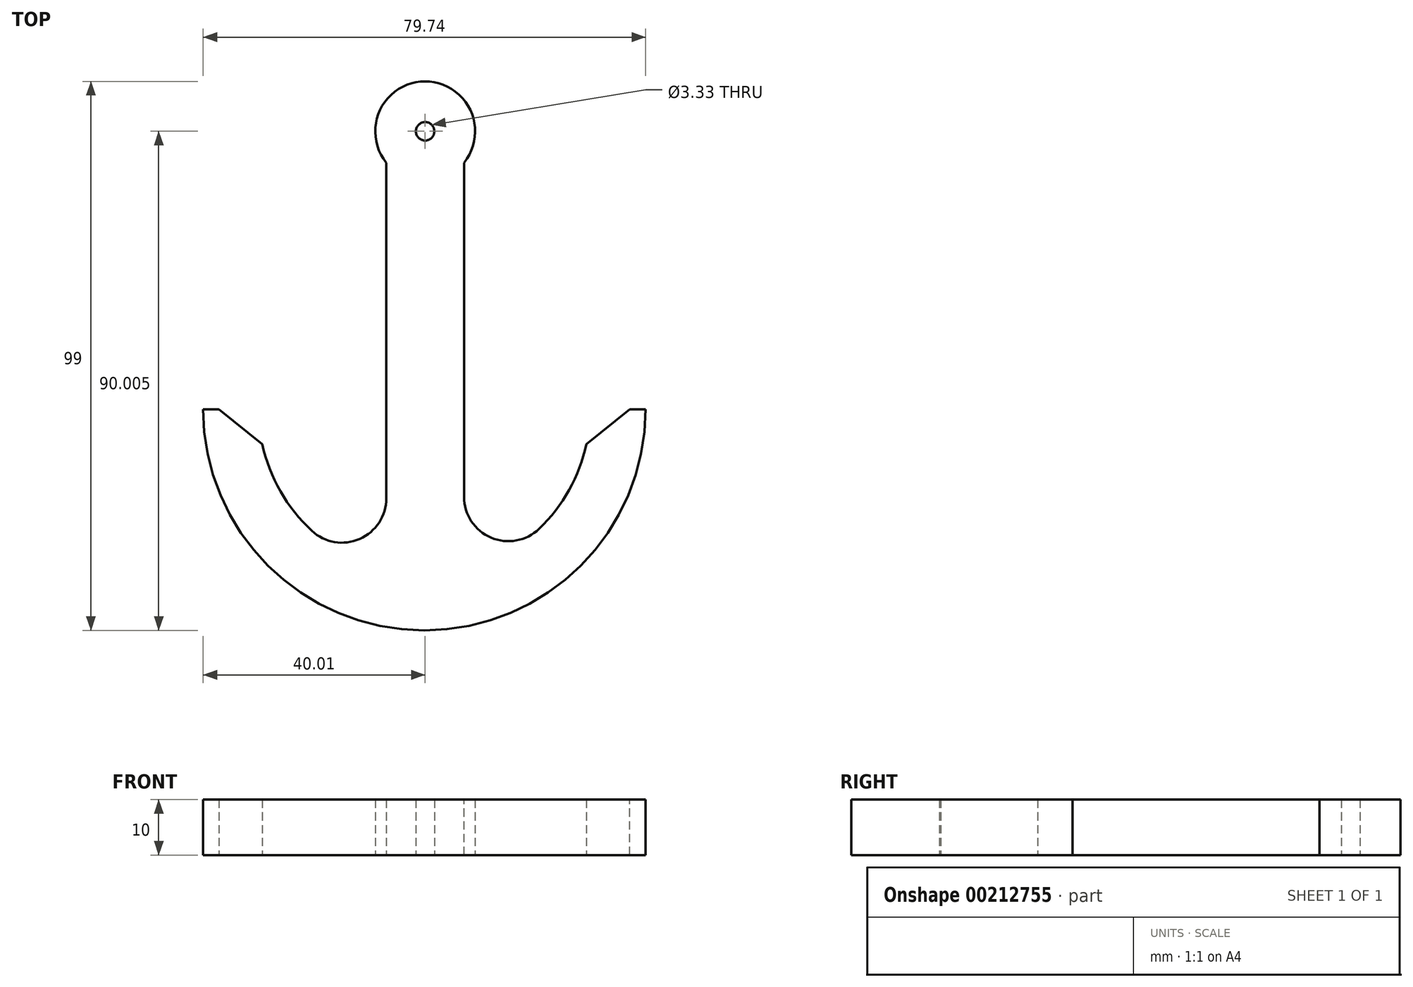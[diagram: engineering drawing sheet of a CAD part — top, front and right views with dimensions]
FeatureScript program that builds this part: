
annotation { "Feature Type Name" : "Feature", "Feature Type Description" : "" }
export const myFeature = defineFeature(function(context is Context, id is Id, definition is map)
    precondition{}
    {
        {
            assignVariable(context, id + "F0", {"name" : "w", "anyValue" : 10});
        }
        {
            var Q0;
            Q0=qCreatedBy(makeId("Top.planeOp"),FACE);
            var sketch = newSketch(context, id + "F1", { "sketchPlane" : qUnion([Q0])});
            skLineSegment(sketch, "E0.bottom", {"start": v(-7, 48.96) * mm, "end": v(7, 48.96) * mm});
            skLineSegment(sketch, "E0.left", {"start": v(-7, 48.96) * mm, "end": v(-7, -35.9) * mm});
            skLineSegment(sketch, "E0.right", {"start": v(7, 48.96) * mm, "end": v(7, -35.83) * mm});
            skCircle(sketch, "E1", {"center": v(0, 43.3) * mm, "radius": 9 * mm});
            skPoint(sketch, "E1.centerSnap0", {"position": v(0, 48.96) * mm});
            skCircle(sketch, "E2", {"center": v(0, 43.3) * mm, "radius": 1.67 * mm});
            skLineSegment(sketch, "E3", {"start": v(39.73, -6.82) * mm, "end": v(39.73, -6.82) * mm});
            skPoint(sketch, "E4", {"position": v(0, -46.7) * mm});
            skPoint(sketch, "E5", {"position": v(-40.01, -6.82) * mm});
            skLineSegment(sketch, "E6", {"start": v(-39.64, -6.82) * mm, "end": v(-40.01, -6.82) * mm});
            skArc(sketch, "E7", {"start": v(-40.01, -6.82) * mm, "mid": v(-0.14, -46.7) * mm, "end": v(39.73, -6.82) * mm});
            skLineSegment(sketch, "E8", {"start": v(-30.01, -6.82) * mm, "end": v(-39.64, -6.82) * mm});
            skArc(sketch, "E9", {"start": v(-30.01, -6.82) * mm, "mid": v(-0.14, -36.7) * mm, "end": v(29.73, -6.82) * mm});
            skLineSegment(sketch, "E10", {"start": v(29.73, -6.82) * mm, "end": v(39.73, -6.82) * mm});
            skPoint(sketch, "E11", {"position": v(-0.14, -36.7) * mm});
            skSolve(sketch);
        }
        {
            var Q0;
            {var subQ5=sQuery(id+"F1.wireOp",EDGE,"E0.bottom");Q0=makeQuery(id+"F1.imprint","IMPRINT",FACE,{"disambiguationData":[TD([[makeQuery(id+"F1.imprint","IMPRINT",EDGE,{"derivedFrom":subQ5}),-1.0]])]});}
            var Q1;
            {var subQ0=sQuery(id+"F1.wireOp",EDGE,"E0.bottom");Q1=makeQuery(id+"F1.imprint","IMPRINT",FACE,{"disambiguationData":[TD([[makeQuery(id+"F1.imprint","IMPRINT",EDGE,{"derivedFrom":subQ0}),1.0]])]});}
            var Q2;
            {var subQ0=sQuery(id+"F1.wireOp",EDGE,"E1");var subQ1=sQuery(id+"F1.wireOp",EDGE,"E0.left");var subQ2=makeQuery(id+"F1.imprint","INTERSECT",VERTEX,{"derivedFrom":[subQ1,subQ0]});Q2=makeQuery(id+"F1.imprint","IMPRINT",FACE,{"disambiguationData":[TD([[makeQuery(id+"F1.imprint","IMPRINT",EDGE,{"disambiguationData":[TD([[subQ2,-1.0]])],"derivedFrom":subQ1}),1.0]])]});}
            var Q3;
            {var subQ0=sQuery(id+"F1.wireOp",EDGE,"TjiRBAFt-rIbT-Rtpd-q4Hv-UdDr9JeEh51r");var subQ1=sQuery(id+"F1.wireOp",EDGE,"E0.left");var subQ2=makeQuery(id+"F1.imprint","INTERSECT",VERTEX,{"disambiguationData":[OD(0.0)],"derivedFrom":[subQ1,subQ0]});Q3=makeQuery(id+"F1.imprint","IMPRINT",FACE,{"disambiguationData":[TD([[makeQuery(id+"F1.imprint","IMPRINT",EDGE,{"disambiguationData":[TD([[subQ2,1.0]])],"derivedFrom":subQ1}),1.0]])]});}
            var Q4;
            {var subQ0=sQuery(id+"F1.wireOp",EDGE,"TjiRBAFt-rIbT-Rtpd-q4Hv-UdDr9JeEh51r");var subQ1=sQuery(id+"F1.wireOp",EDGE,"E0.left");var subQ2=makeQuery(id+"F1.imprint","INTERSECT",VERTEX,{"disambiguationData":[OD(1.0)],"derivedFrom":[subQ1,subQ0]});Q4=makeQuery(id+"F1.imprint","IMPRINT",FACE,{"disambiguationData":[TD([[makeQuery(id+"F1.imprint","IMPRINT",EDGE,{"disambiguationData":[TD([[subQ2,-1.0]])],"derivedFrom":subQ1}),1.0]])]});}
            var Q5;
            {var subQ1=sQuery(id+"F1.wireOp",EDGE,"E0.left");var subQ5=sQuery(id+"F1.wireOp",EDGE,"KmF6qriy-v43V-YwKp-XvIB-jkBJgwhcMQSk");var subQ9=makeQuery(id+"F1.imprint","INTERSECT",VERTEX,{"derivedFrom":[subQ1,subQ5]});Q5=makeQuery(id+"F1.imprint","IMPRINT",FACE,{"disambiguationData":[TD([[makeQuery(id+"F1.imprint","IMPRINT",EDGE,{"disambiguationData":[TD([[subQ9,-1.0]])],"derivedFrom":subQ1}),1.0]])]});}
            var Q6;
            {var subQ0=sQuery(id+"F1.wireOp",EDGE,"E1");var subQ1=sQuery(id+"F1.wireOp",EDGE,"E0.right");var subQ2=makeQuery(id+"F1.imprint","INTERSECT",VERTEX,{"derivedFrom":[subQ1,subQ0]});Q6=makeQuery(id+"F1.imprint","IMPRINT",FACE,{"disambiguationData":[TD([[makeQuery(id+"F1.imprint","IMPRINT",EDGE,{"disambiguationData":[TD([[subQ2,-1.0]])],"derivedFrom":subQ1}),-1.0]])]});}
            var Q7;
            {var subQ0=sQuery(id+"F1.wireOp",EDGE,"TjiRBAFt-rIbT-Rtpd-q4Hv-UdDr9JeEh51r");var subQ1=sQuery(id+"F1.wireOp",EDGE,"E1");var subQ2=makeQuery(id+"F1.imprint","INTERSECT",VERTEX,{"disambiguationData":[OD(0.0)],"derivedFrom":[subQ1,subQ0]});Q7=makeQuery(id+"F1.imprint","IMPRINT",FACE,{"disambiguationData":[TD([[makeQuery(id+"F1.imprint","IMPRINT",EDGE,{"disambiguationData":[TD([[subQ2,-1.0]])],"derivedFrom":subQ1}),1.0]])]});}
            var Q8;
            {var subQ0=sQuery(id+"F1.wireOp",EDGE,"E3");var subQ1=sQuery(id+"F1.wireOp",EDGE,"E0.left");var subQ2=makeQuery(id+"F1.imprint","INTERSECT",VERTEX,{"derivedFrom":[subQ1,subQ0]});Q8=makeQuery(id+"F1.imprint","IMPRINT",FACE,{"disambiguationData":[TD([[makeQuery(id+"F1.imprint","IMPRINT",EDGE,{"disambiguationData":[TD([[subQ2,-1.0]])],"derivedFrom":subQ1}),1.0]])]});}
            var Q9;
            {var subQ0=sQuery(id+"F1.wireOp",EDGE,"E3");var subQ1=sQuery(id+"F1.wireOp",EDGE,"E0.right");var subQ2=makeQuery(id+"F1.imprint","INTERSECT",VERTEX,{"derivedFrom":[subQ1,subQ0]});Q9=makeQuery(id+"F1.imprint","IMPRINT",FACE,{"disambiguationData":[TD([[makeQuery(id+"F1.imprint","IMPRINT",EDGE,{"disambiguationData":[TD([[subQ2,-1.0]])],"derivedFrom":subQ1}),-1.0]])]});}
            var Q10;
            {var subQ2=sQuery(id+"F1.wireOp",EDGE,"MNqs9SMt-crvg-llG4-YDsR-waINOACBQYCp");var subQ7=sQuery(id+"F1.wireOp",EDGE,"KmF6qriy-v43V-YwKp-XvIB-jkBJgwhcMQSk");var subQ9=makeQuery(id+"F1.imprint","INTERSECT",VERTEX,{"derivedFrom":[subQ7,subQ2]});Q10=makeQuery(id+"F1.imprint","IMPRINT",FACE,{"disambiguationData":[TD([[makeQuery(id+"F1.imprint","IMPRINT",EDGE,{"disambiguationData":[TD([[subQ9,-1.0]])],"derivedFrom":subQ7}),1.0]])]});}
            var Q11;
            {var subQ2=sQuery(id+"F1.wireOp",EDGE,"E3");var subQ4=sQuery(id+"F1.wireOp",EDGE,"KmF6qriy-v43V-YwKp-XvIB-jkBJgwhcMQSk");var subQ5=makeQuery(id+"F1.imprint","INTERSECT",VERTEX,{"disambiguationData":[OD(1.0)],"derivedFrom":[subQ4,subQ2]});Q11=makeQuery(id+"F1.imprint","IMPRINT",FACE,{"disambiguationData":[TD([[makeQuery(id+"F1.imprint","IMPRINT",EDGE,{"disambiguationData":[TD([[subQ5,-1.0]])],"derivedFrom":subQ4}),1.0]])]});}
            var Q12;
            {var subQ0=sQuery(id+"F1.wireOp",EDGE,"E1");var subQ3=sQuery(id+"F1.wireOp",EDGE,"KmF6qriy-v43V-YwKp-XvIB-jkBJgwhcMQSk");var subQ5=makeQuery(id+"F1.imprint","INTERSECT",VERTEX,{"disambiguationData":[OD(1.0)],"derivedFrom":[subQ0,subQ3]});Q12=makeQuery(id+"F1.imprint","IMPRINT",FACE,{"disambiguationData":[TD([[makeQuery(id+"F1.imprint","IMPRINT",EDGE,{"disambiguationData":[TD([[subQ5,-1.0]])],"derivedFrom":subQ3}),-1.0]])]});}
            var Q13;
            {var subQ0=sQuery(id+"F1.wireOp",EDGE,"E1");var subQ3=sQuery(id+"F1.wireOp",EDGE,"KmF6qriy-v43V-YwKp-XvIB-jkBJgwhcMQSk");var subQ5=makeQuery(id+"F1.imprint","INTERSECT",VERTEX,{"disambiguationData":[OD(0.0)],"derivedFrom":[subQ0,subQ3]});Q13=makeQuery(id+"F1.imprint","IMPRINT",FACE,{"disambiguationData":[TD([[makeQuery(id+"F1.imprint","IMPRINT",EDGE,{"disambiguationData":[TD([[subQ5,1.0]])],"derivedFrom":subQ3}),-1.0]])]});}
            var Q14;
            {var subQ0=sQuery(id+"F1.wireOp",EDGE,"E1");var subQ1=sQuery(id+"F1.wireOp",EDGE,"E0.left");var subQ3=makeQuery(id+"F1.imprint","INTERSECT",VERTEX,{"derivedFrom":[subQ1,subQ0]});Q14=makeQuery(id+"F1.imprint","IMPRINT",FACE,{"disambiguationData":[TD([[makeQuery(id+"F1.imprint","IMPRINT",EDGE,{"disambiguationData":[TD([[subQ3,1.0]])],"derivedFrom":subQ1}),-1.0]])]});}
            var Q15;
            Q15=makeQuery(id+"F1.imprint","IMPRINT",FACE,{"disambiguationData":[TD([[makeQuery(id+"F1.imprint","IMPRINT",EDGE,{"derivedFrom":sQuery(id+"F1.wireOp",EDGE,"E7")}),1.0]])]});
            extrude(context, id + "F2", {"entities" : qUnion([Q0, Q1, Q2, Q3, Q4, Q5, Q6, Q7, Q8, Q9, Q10, Q11, Q12, Q13, Q14, Q15]), "depth" : (getVariable(context, 'w')) * mm});
        }
        {
            var Q0;
            Q0=makeQuery(id+"F2.opExtrude","SWEPT_EDGE",EDGE,{"disambiguationData":[OSD([sQuery(id+"F1.wireOp",EDGE,"E8"),sQuery(id+"F1.wireOp",EDGE,"E9")])]});
            var Q1;
            Q1=makeQuery(id+"F2.opExtrude","SWEPT_EDGE",EDGE,{"disambiguationData":[OSD([sQuery(id+"F1.wireOp",EDGE,"E9"),sQuery(id+"F1.wireOp",EDGE,"E10")])]});
            chamfer(context, id + "F3", {"entities" : qUnion([Q0, Q1]), "width" : 8 * mm, "tangentPropagation" : true});
        }
        {
            var Q0;
            Q0=makeQuery(id+"F2.opExtrude","SWEPT_EDGE",EDGE,{"disambiguationData":[OSD([sQuery(id+"F1.wireOp",EDGE,"E0.left"),sQuery(id+"F1.wireOp",EDGE,"E9")])]});
            var Q1;
            Q1=makeQuery(id+"F2.opExtrude","SWEPT_EDGE",EDGE,{"disambiguationData":[OSD([sQuery(id+"F1.wireOp",EDGE,"E0.right"),sQuery(id+"F1.wireOp",EDGE,"E9")])]});
            fillet(context, id + "F4", {"entities" : qUnion([Q0, Q1]), "radius" : 8 * mm, "tangentPropagation" : true, "allowEdgeOverflow" : false});
        }
        {
            var Q0;
            Q0=qCreatedBy(makeId("Right.planeOp"),FACE);
            cPlane(context, id + "F5", {"entities" : qUnion([Q0]), "cplaneType" : CPlaneType.OFFSET, "offset" : 50 * mm, "oppositeDirection" : true, "width" : 150 * mm, "height" : 150 * mm});
        }
    });
